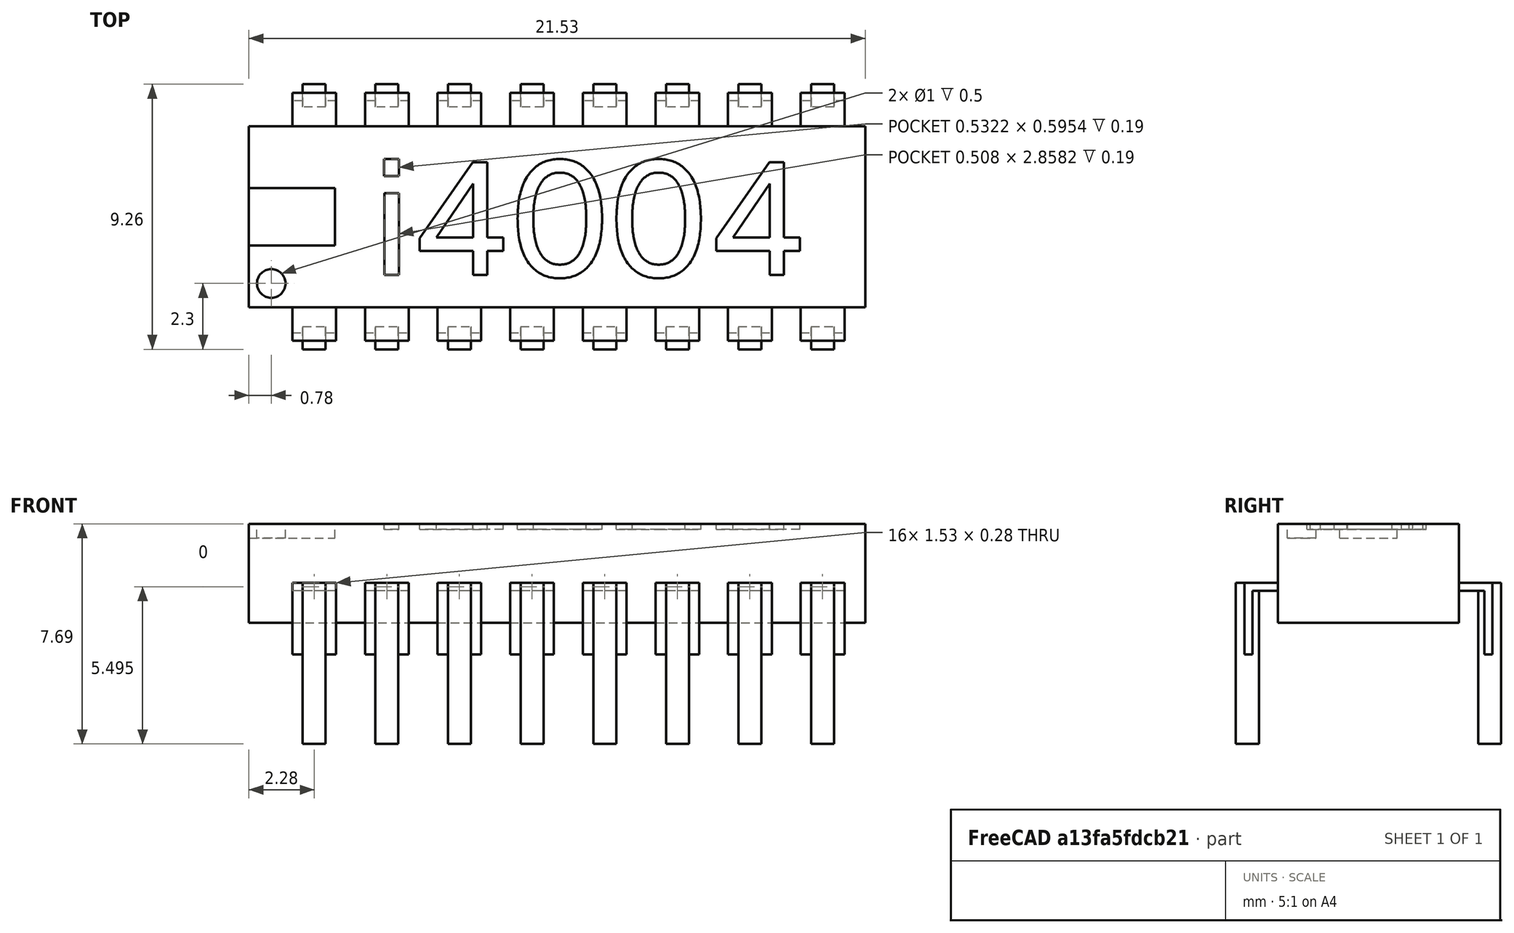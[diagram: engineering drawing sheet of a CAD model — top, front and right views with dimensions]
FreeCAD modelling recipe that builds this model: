
FCSTD DOCUMENT  (FreeCAD 0.18R4 (GitTag))
Label: Chip_i4004_FatLeg
License: All rights reserved
LicenseURL: http://en.wikipedia.org/wiki/All_rights_reserved
objects: Part::Feature×20, Part::Box×5, Part::MultiFuse×4, Part::Cut×2, Part::Cylinder×1, Part::Part2DObjectPython×1, Part::Extrusion×1
note: 34 computed .brp shape members not serialized (recipe doc carries the construction recipe); baked Part::Feature solids carry a one-line shape summary decoded from their .brp

FEATURE [Part::Box] Box001  label="ChipBody_block"
  AttacherType = Attacher::AttachEngine3D
  Height = 3.46
  Length = 21.53
  Placement = pos=(-2.28,1.17,4.23) rot=(0,0,1;0rad)
  Width = 6.32
FEATURE [Part::Box] Box002  label="Cube001"
  AttacherType = Attacher::AttachEngine3D
  Height = 5.63
  Length = 0.8
  Placement = pos=(-0.4,-0.3,0) rot=(0,0,1;0rad)
  Width = 0.8
FEATURE [Part::Box] Box003  label="Cube002"
  AttacherType = Attacher::AttachEngine3D
  Height = 2.5
  Length = 1.53
  Placement = pos=(-0.765,0,3.13) rot=(0,0,1;0rad)
  Width = 0.28
FEATURE [Part::Box] Box004  label="Cube003"
  AttacherType = Attacher::AttachEngine3D
  Height = 0.28
  Length = 1.53
  Placement = pos=(-0.765,0,5.355) rot=(0,0,1;0rad)
  Width = 1.17
FEATURE [Part::MultiFuse] Fusion  label="ChipLegFat (Model)"
  Shapes = -> [Box002,Box003,Box004]
FEATURE [Part::Box] Box005  label="Cube"
  AttacherType = Attacher::AttachEngine3D
  Height = 0.5
  Length = 3
  Placement = pos=(-2.28,3.33,7.19) rot=(0,0,1;0rad)
  Width = 2
FEATURE [Part::Cylinder] Cylinder
  Angle = 360
  AttacherType = Attacher::AttachEngine3D
  Height = 0.5
  Placement = pos=(-1.5,2,7.19) rot=(0,0,1;0rad)
  Radius = 0.5
FEATURE [Part::Part2DObjectPython] ShapeString  # Draft 2D object (typed FeaturePython)
  FontFile = <userpath>/Desktop/Intel Clear Arabic Regular.ttf
  Placement = pos=(2,2.3,0) rot=(0,0,1;0rad)
  Size = 5
  String = i4004
  Tracking = 0
FEATURE [Part::Extrusion] Extrude  label="i4004"
  Base = -> ShapeString
  Dir = (0,0,1)
  DirMode = 2
  FaceMakerClass = Part::FaceMakerBullseye
  LengthFwd = 0.2
  LengthRev = 0
  Placement = pos=(0,0,7.5) rot=(0,0,1;0rad)
  Solid = false
  Symmetric = false
FEATURE [Part::MultiFuse] Fusion003
  Shapes = -> [Box005,Cylinder]
FEATURE [Part::Cut] Cut  label="ChipBody"
  Base = -> Box001
  Tool = -> Fusion003
FEATURE [Part::Feature] Fusion_solid016  label="ChipLegFat (Solid)"
  shape: bbox 1.53 x 1.47 x 5.635 mm, 24 faces (baked)
FEATURE [Part::Feature] Fusion_solid017  label="ChipLegFat_00"
  shape: bbox 1.53 x 1.47 x 5.635 mm, 24 faces (baked)
FEATURE [Part::Feature] Fusion_solid018  label="ChipLegFat_01"
  Placement = pos=(0,8.66,0) rot=(0,0,1;3.14159rad)
  shape: bbox 1.53 x 1.47 x 5.635 mm, 24 faces (baked)
FEATURE [Part::Feature] Fusion_solid019  label="ChipLegFat_02"
  Placement = pos=(2.54,0,0) rot=(0,0,1;0rad)
  shape: bbox 1.53 x 1.47 x 5.635 mm, 24 faces (baked)
FEATURE [Part::Feature] Fusion_solid020  label="ChipLegFat_03"
  Placement = pos=(2.54,8.66,0) rot=(0,0,1;3.14159rad)
  shape: bbox 1.53 x 1.47 x 5.635 mm, 24 faces (baked)
FEATURE [Part::Feature] Fusion_solid021  label="ChipLegFat_04"
  Placement = pos=(5.07,0,0) rot=(0,0,1;0rad)
  shape: bbox 1.53 x 1.47 x 5.635 mm, 24 faces (baked)
FEATURE [Part::Feature] Fusion_solid022  label="ChipLegFat_05"
  Placement = pos=(5.07,8.66,0) rot=(0,0,1;3.14159rad)
  shape: bbox 1.53 x 1.47 x 5.635 mm, 24 faces (baked)
FEATURE [Part::Feature] Fusion_solid023  label="ChipLegFat_06"
  Placement = pos=(7.61,0,0) rot=(0,0,1;0rad)
  shape: bbox 1.53 x 1.47 x 5.635 mm, 24 faces (baked)
FEATURE [Part::Feature] Fusion_solid024  label="ChipLegFat_07"
  Placement = pos=(7.61,8.66,0) rot=(0,0,1;3.14159rad)
  shape: bbox 1.53 x 1.47 x 5.635 mm, 24 faces (baked)
FEATURE [Part::Feature] Fusion_solid025  label="ChipLegFat_08"
  Placement = pos=(10.15,0,0) rot=(0,0,1;0rad)
  shape: bbox 1.53 x 1.47 x 5.635 mm, 24 faces (baked)
FEATURE [Part::Feature] Fusion_solid026  label="ChipLegFat_09"
  Placement = pos=(10.15,8.66,0) rot=(0,0,1;3.14159rad)
  shape: bbox 1.53 x 1.47 x 5.635 mm, 24 faces (baked)
FEATURE [Part::Feature] Fusion_solid027  label="ChipLegFat_10"
  Placement = pos=(12.69,0,0) rot=(0,0,1;0rad)
  shape: bbox 1.53 x 1.47 x 5.635 mm, 24 faces (baked)
FEATURE [Part::Feature] Fusion_solid028  label="ChipLegFat_11"
  Placement = pos=(12.69,8.66,0) rot=(0,0,1;3.14159rad)
  shape: bbox 1.53 x 1.47 x 5.635 mm, 24 faces (baked)
FEATURE [Part::Feature] Fusion_solid029  label="ChipLegFat_12"
  Placement = pos=(15.22,0,0) rot=(0,0,1;0rad)
  shape: bbox 1.53 x 1.47 x 5.635 mm, 24 faces (baked)
FEATURE [Part::Feature] Fusion_solid030  label="ChipLegFat_13"
  Placement = pos=(15.22,8.66,0) rot=(0,0,1;3.14159rad)
  shape: bbox 1.53 x 1.47 x 5.635 mm, 24 faces (baked)
FEATURE [Part::Feature] Fusion_solid031  label="ChipLegFat_14"
  Placement = pos=(17.76,0,0) rot=(0,0,1;0rad)
  shape: bbox 1.53 x 1.47 x 5.635 mm, 24 faces (baked)
FEATURE [Part::Feature] Fusion_solid032  label="ChipLegFat_15"
  Placement = pos=(17.76,8.66,0) rot=(0,0,1;3.14159rad)
  shape: bbox 1.53 x 1.47 x 5.635 mm, 24 faces (baked)
FEATURE [Part::MultiFuse] Fusion004
  Shapes = -> [Fusion_solid017,Fusion_solid032,Fusion_solid018,Fusion_solid019,Fusion_solid024,Fusion_solid027,Fusion_solid031,Fusion_solid029,Fusion_solid022,Fusion_solid020,Fusion_solid021,Fusion_solid026,Fusion_solid023,Fusion_solid025,Fusion_solid030,Fusion_solid028]
FEATURE [Part::MultiFuse] Fusion005  label="Chip_FatLeg (Model)"
  Shapes = -> [Cut,Fusion004]
FEATURE [Part::Feature] Fusion005_solid  label="Chip_FatLeg (Solid)"
  shape: bbox 21.53 x 9.26 x 7.69 mm, 380 faces (baked)
FEATURE [Part::Feature] Fusion005_solid001  label="i4004_FatLeg"
  shape: bbox 21.53 x 9.26 x 7.69 mm, 380 faces (baked)
FEATURE [Part::Cut] Cut001  label="i4004_FatLeg (Model)"
  Base = -> Fusion005_solid001
  Tool = -> Extrude
FEATURE [Part::Feature] Cut001_solid  label="i4004_FatLeg (Solid)"
  shape: bbox 21.53 x 9.26 x 7.69 mm, 458 faces (baked)
